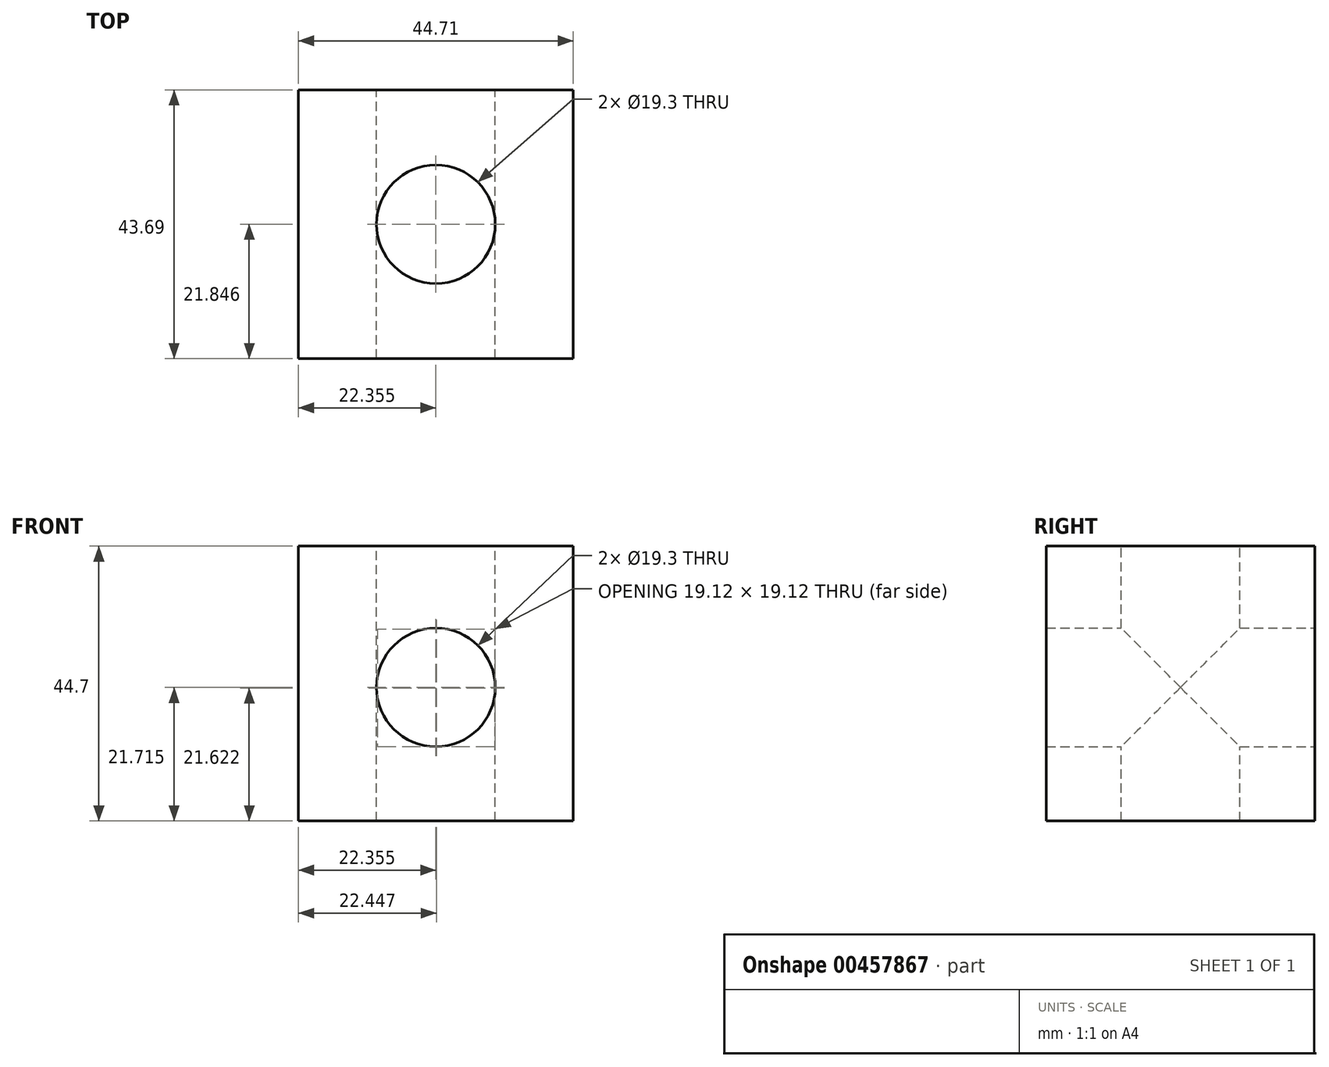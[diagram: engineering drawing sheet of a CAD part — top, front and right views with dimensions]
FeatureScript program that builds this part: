
annotation { "Feature Type Name" : "Feature", "Feature Type Description" : "" }
export const myFeature = defineFeature(function(context is Context, id is Id, definition is map)
    precondition{}
    {
        {
            var Q0;
            Q0=qCreatedBy(makeId("Front.planeOp"),FACE);
            var sketch = newSketch(context, id + "F0", { "sketchPlane" : qUnion([Q0])});
            skLineSegment(sketch, "E0.bottom", {"start": v(-39.48, 25.91) * mm, "end": v(5.23, 25.91) * mm});
            skLineSegment(sketch, "E0.top", {"start": v(-39.48, -18.8) * mm, "end": v(5.23, -18.8) * mm});
            skLineSegment(sketch, "E0.left", {"start": v(-39.48, 25.91) * mm, "end": v(-39.48, -18.8) * mm});
            skCircle(sketch, "E1", {"center": v(-17.13, 2.92) * mm, "radius": 9.65 * mm});
            skPoint(sketch, "E2.orphan", {"position": v(5.23, 25.91) * mm});
            skLineSegment(sketch, "E3", {"start": v(5.23, 25.91) * mm, "end": v(5.23, -18.8) * mm});
            skSolve(sketch);
        }
        {
            var Q0;
            Q0=qSketchRegion(id+"F0",true);
            extrude(context, id + "F1", {"entities" : qUnion([Q0]), "depth" : 43.69 * mm});
        }
        {
            var Q0;
            Q0=makeQuery(id+"F1.opExtrude","SWEPT_FACE",FACE,{"disambiguationData":[OSD([sQuery(id+"F0.wireOp",EDGE,"E0.bottom")])]});
            var sketch = newSketch(context, id + "F2", { "sketchPlane" : qUnion([Q0])});
            skLineSegment(sketch, "E4", {"start": v(-17.13, 0) * mm, "end": v(-17.13, -43.69) * mm, "construction": true});
            skCircle(sketch, "E5", {"center": v(-17.13, -21.84) * mm, "radius": 9.65 * mm});
            skSolve(sketch);
        }
        {
            var Q0;
            Q0=makeQuery(id+"F2.imprint","IMPRINT",FACE,{"disambiguationData":[TD([[makeQuery(id+"F2.imprint","IMPRINT",EDGE,{"derivedFrom":sQuery(id+"F2.wireOp",EDGE,"E5")}),1.0]])]});
            extrude(context, id + "F3", {"entities" : qUnion([Q0]), "operationType" : NewBodyOperationType.REMOVE, "endBound" : BoundingType.THROUGH_ALL, "oppositeDirection" : true, "depth" : 25.4 * mm});
        }
    });
